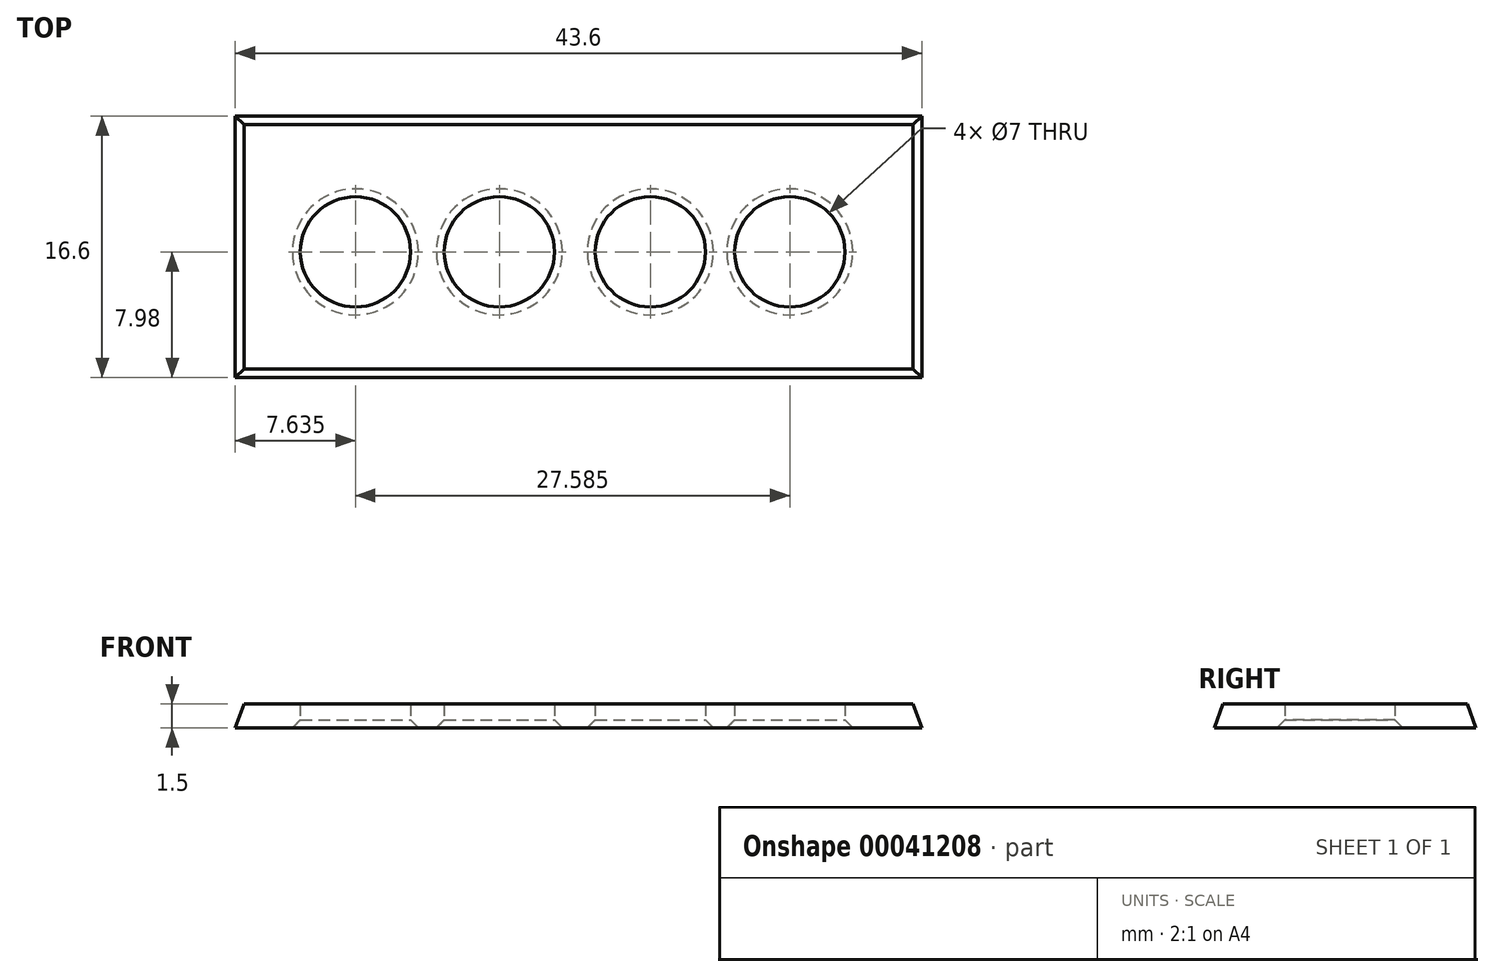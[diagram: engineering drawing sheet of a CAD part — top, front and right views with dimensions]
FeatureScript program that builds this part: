
annotation { "Feature Type Name" : "Feature", "Feature Type Description" : "" }
export const myFeature = defineFeature(function(context is Context, id is Id, definition is map)
    precondition{}
    {
        {
            var Q0;
            Q0=qCreatedBy(makeId("Top.planeOp"),FACE);
            var sketch = newSketch(context, id + "F0", { "sketchPlane" : qUnion([Q0])});
            skLineSegment(sketch, "E0.bottom", {"start": v(-35.22, 4.6) * mm, "end": v(8.38, 4.6) * mm});
            skLineSegment(sketch, "E0.top", {"start": v(-35.22, -12) * mm, "end": v(8.38, -12) * mm});
            skLineSegment(sketch, "E0.left", {"start": v(-35.22, 4.6) * mm, "end": v(-35.22, -12) * mm});
            skLineSegment(sketch, "E0.right", {"start": v(8.38, 4.6) * mm, "end": v(8.38, -12) * mm});
            skCircle(sketch, "E1", {"center": v(-27.59, -4.03) * mm, "radius": 2.87 * mm, "construction": true});
            skCircle(sketch, "E2", {"center": v(-18.45, -4.03) * mm, "radius": 2.87 * mm, "construction": true});
            skCircle(sketch, "E3", {"center": v(-8.86, -4.03) * mm, "radius": 2.87 * mm, "construction": true});
            skCircle(sketch, "E4", {"center": v(0, -4.03) * mm, "radius": 2.87 * mm, "construction": true});
            skSolve(sketch);
        }
        {
            var Q0;
            Q0=makeQuery(id+"F0.imprint","IMPRINT",FACE,{"disambiguationData":[TD([[makeQuery(id+"F0.imprint","IMPRINT",EDGE,{"derivedFrom":sQuery(id+"F0.wireOp",EDGE,"E0.bottom")}),-1.0]])]});
            extrude(context, id + "F1", {"entities" : qUnion([Q0]), "depth" : 1.5 * mm, "hasDraft" : true, "draftAngle" : 20 * degree, "draftPullDirection" : true});
        }
        {
            var Q0;
            Q0=sQuery(id+"F0.wireOp",VERTEX,"E1.center");
            var Q1;
            Q1=sQuery(id+"F0.wireOp",VERTEX,"E2.center");
            var Q2;
            Q2=sQuery(id+"F0.wireOp",VERTEX,"E3.center");
            var Q3;
            Q3=sQuery(id+"F0.wireOp",VERTEX,"E4.center");
            var Q4;
            Q4=makeQuery(id+"F1.opExtrude","SWEPT_BODY",BODY,{"disambiguationData":[OSD([sQuery(id+"F0.wireOp",EDGE,"E0.bottom"),sQuery(id+"F0.wireOp",EDGE,"E0.top"),sQuery(id+"F0.wireOp",EDGE,"E0.left"),sQuery(id+"F0.wireOp",EDGE,"E0.right")])]});
            hole(context, id + "F2", {"style" : HoleStyle.C_SINK, "holeDiameter" : 7 * mm, "cSinkDiameter" : 8 * mm, "endStyle" : HoleEndStyle.THROUGH, "oppositeDirection" : true, "locations" : qUnion([Q0, Q1, Q2, Q3]), "scope" : qUnion([Q4]), "cSinkAngle" : 90 * degree});
        }
    });
